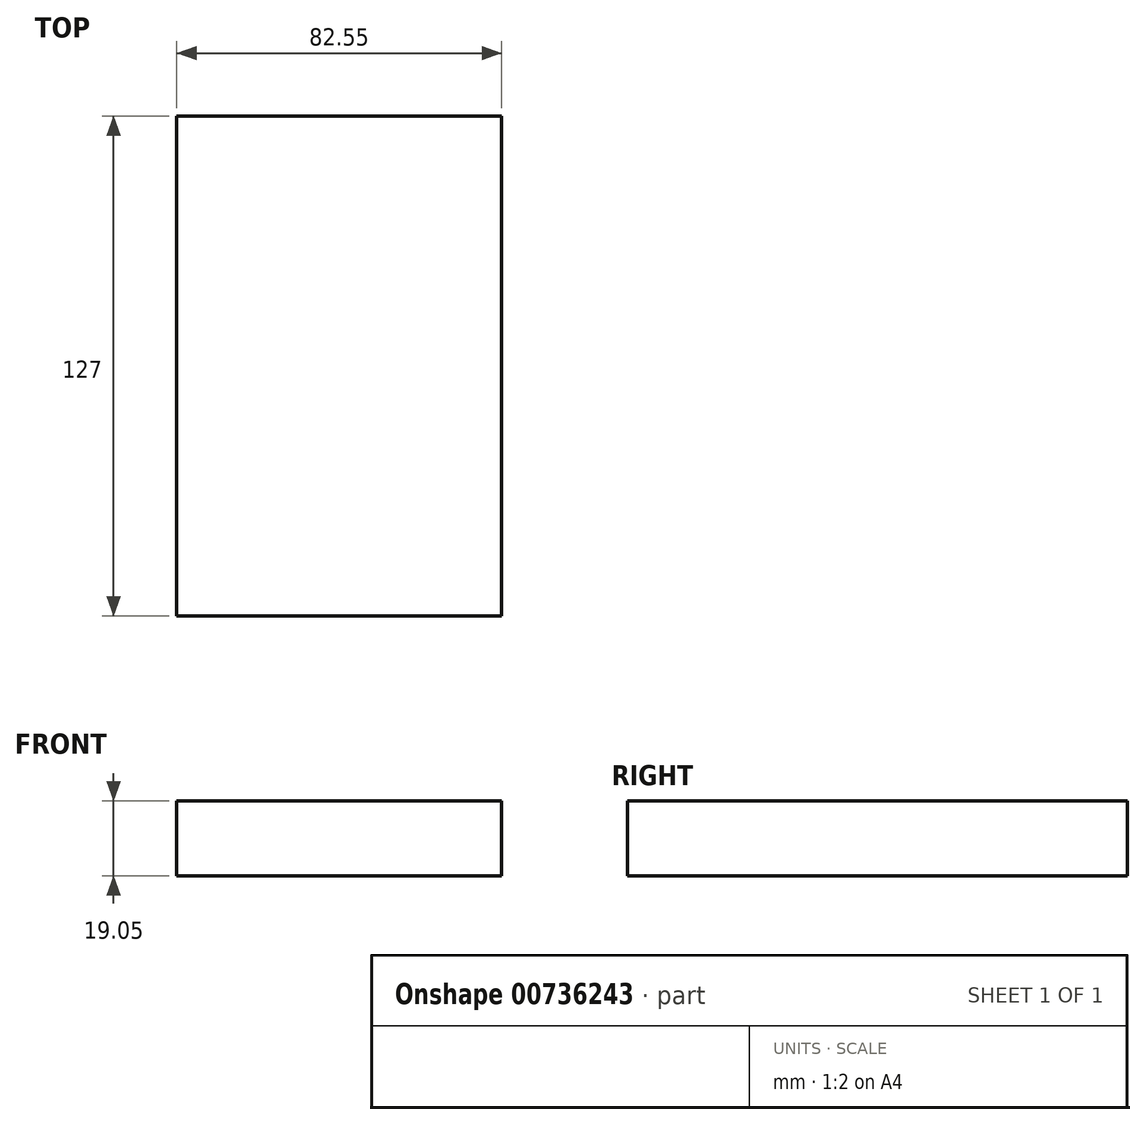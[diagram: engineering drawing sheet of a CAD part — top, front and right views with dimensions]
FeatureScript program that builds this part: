
annotation { "Feature Type Name" : "Feature", "Feature Type Description" : "" }
export const myFeature = defineFeature(function(context is Context, id is Id, definition is map)
    precondition{}
    {
        {
            var Q0;
            Q0=qCreatedBy(makeId("Front.planeOp"),FACE);
            var sketch = newSketch(context, id + "F0", { "sketchPlane" : qUnion([Q0])});
            skLineSegment(sketch, "E0.bottom", {"start": v(41.28, 9.72) * mm, "end": v(-41.28, 9.72) * mm});
            skLineSegment(sketch, "E0.top", {"start": v(41.27, 28.77) * mm, "end": v(-41.27, 28.77) * mm});
            skLineSegment(sketch, "E0.left", {"start": v(41.28, 9.72) * mm, "end": v(41.28, 28.77) * mm});
            skLineSegment(sketch, "E0.right", {"start": v(-41.28, 9.72) * mm, "end": v(-41.28, 28.77) * mm});
            skPoint(sketch, "E0.middle", {"position": v(0, 19.24) * mm});
            skLineSegment(sketch, "E1", {"start": v(41.28, 28.77) * mm, "end": v(41.28, 46.24) * mm});
            skArc(sketch, "E2", {"start": v(41.28, 46.24) * mm, "mid": v(45.92, 57.47) * mm, "end": v(57.15, 62.12) * mm});
            skLineSegment(sketch, "E3", {"start": v(57.15, 62.12) * mm, "end": v(79.17, 62.12) * mm});
            skLineSegment(sketch, "E4.bottom", {"start": v(111.13, 57.34) * mm, "end": v(60.33, 57.34) * mm});
            skLineSegment(sketch, "E4.top", {"start": v(111.13, 85.92) * mm, "end": v(60.33, 85.92) * mm});
            skLineSegment(sketch, "E4.left", {"start": v(111.13, 57.34) * mm, "end": v(111.13, 85.92) * mm});
            skLineSegment(sketch, "E4.right", {"start": v(60.33, 57.34) * mm, "end": v(60.32, 85.92) * mm});
            skPoint(sketch, "E4.middle", {"position": v(85.73, 71.63) * mm});
            skLineSegment(sketch, "E5.0", {"start": v(57.15, 81.17) * mm, "end": v(79.17, 81.17) * mm});
            skArc(sketch, "E5.1", {"start": v(22.23, 46.24) * mm, "mid": v(32.45, 70.94) * mm, "end": v(57.15, 81.17) * mm});
            skLineSegment(sketch, "E5.2", {"start": v(22.23, 28.77) * mm, "end": v(22.23, 46.24) * mm});
            skLineSegment(sketch, "E6", {"start": v(79.17, 57.34) * mm, "end": v(79.17, 85.92) * mm});
            skFitSpline(sketch, "E7", {"points": [v(-41.28, 28.77) * mm, v(57.15, 81.17) * mm], "startDerivative": vector(71.04, 102.76) * mm, "endDerivative": vector(146.67, -11.2) * mm});
            skSolve(sketch);
        }
        {
            var Q0;
            Q0=makeQuery(id+"F0.imprint","IMPRINT",FACE,{"disambiguationData":[TD([[makeQuery(id+"F0.imprint","IMPRINT",EDGE,{"derivedFrom":sQuery(id+"F0.wireOp",EDGE,"E0.bottom")}),-1.0]])]});
            extrude(context, id + "F1", {"entities" : qUnion([Q0]), "endBound" : BoundingType.SYMMETRIC, "depth" : 127 * mm, "offsetDistance" : 25.4 * mm});
        }
    });
